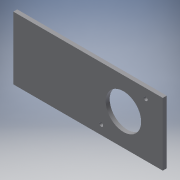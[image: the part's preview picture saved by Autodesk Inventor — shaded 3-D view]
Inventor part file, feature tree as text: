
AUTODESK INVENTOR PART (.ipt)
format: ipt  version: 2016 (Build 200138000, 138)  size: 115,200 bytes
history: native  units: in
note: dims shown in document units (in); Inventor stores cm internally (conversion verified against a paired STEP export)
features: extrude x2, sketch x2
ambient origin geometry x8: Origin, YZ Plane, XZ Plane, XY Plane, X Axis, Y Axis, Z Axis, Center Point
bodies: Solid1 (feature_tree)
feature tree (4):
  extrude  "Extrusion1"  Depth=1.0in
  extrude  "Extrusion2"  Depth=2.0in
  sketch  "Sketch1"  dims[d0=1.125in d1=1.0in]
  sketch  "Sketch2"  dims[d2=1.0in d3=2.0in d4=0.125in d5=0.125in d6=1.0in d7=1.25in d8=3.5in d9=0.7071in d10=0.7071in d11=0.125in d12=0.0in d13=0.2656in d14=0.5in d15=0.5in d16=0.2656in d17=0.5in d18=1.5in d19=0.125in d20=0.0in]
